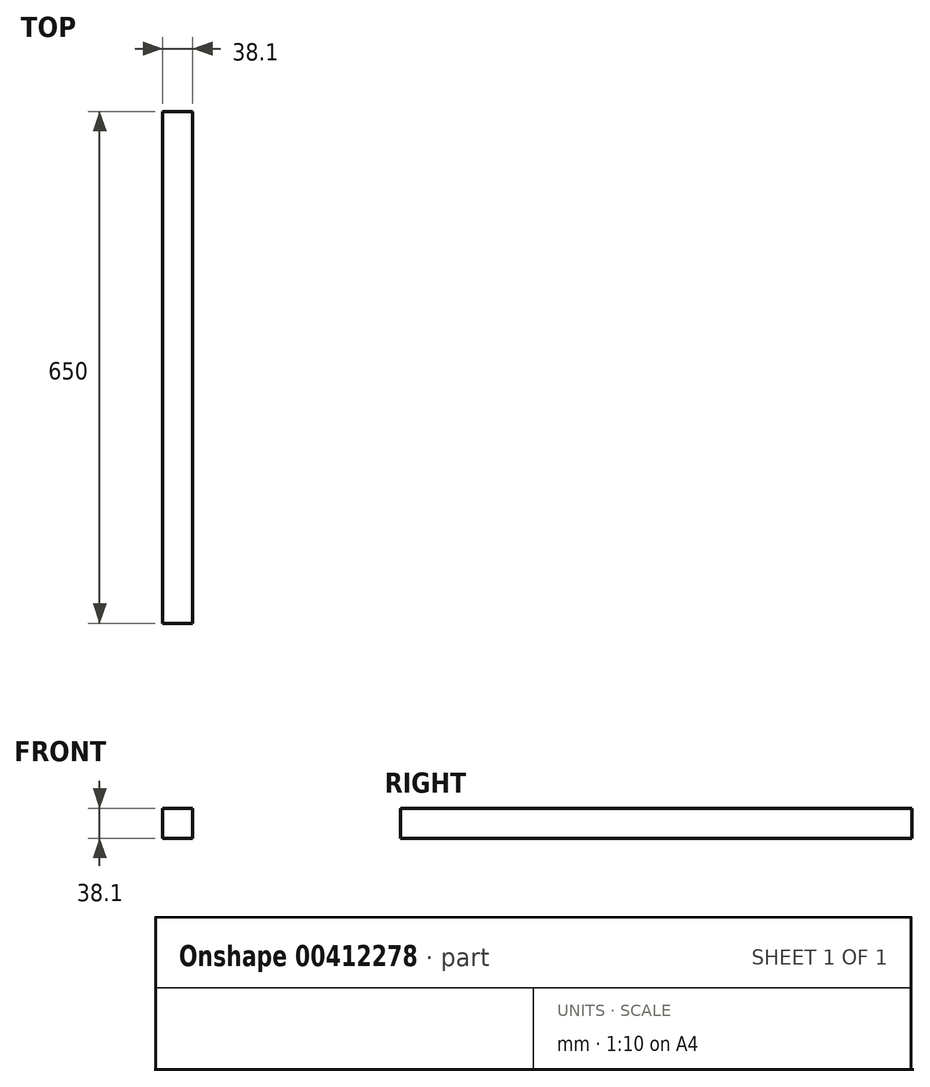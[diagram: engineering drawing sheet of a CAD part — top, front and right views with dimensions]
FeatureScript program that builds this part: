
annotation { "Feature Type Name" : "Feature", "Feature Type Description" : "" }
export const myFeature = defineFeature(function(context is Context, id is Id, definition is map)
    precondition{}
    {
        {
            var Q0;
            Q0=qCreatedBy(makeId("Front.planeOp"),FACE);
            var sketch = newSketch(context, id + "F0", { "sketchPlane" : qUnion([Q0])});
            skLineSegment(sketch, "E0.bottom", {"start": v(-19.05, 38.1) * mm, "end": v(19.05, 38.1) * mm});
            skLineSegment(sketch, "E0.top", {"start": v(-19.05, 0) * mm, "end": v(19.05, 0) * mm});
            skLineSegment(sketch, "E0.left", {"start": v(-19.05, 38.1) * mm, "end": v(-19.05, 0) * mm});
            skLineSegment(sketch, "E0.right", {"start": v(19.05, 38.1) * mm, "end": v(19.05, 0) * mm});
            skSolve(sketch);
        }
        {
            var Q0;
            Q0 = qSketchRegion(id + "F0", true);
            extrude(context, id + "F1", {"entities" : qUnion([Q0]), "depth" : 650 * mm});
        }
    });
